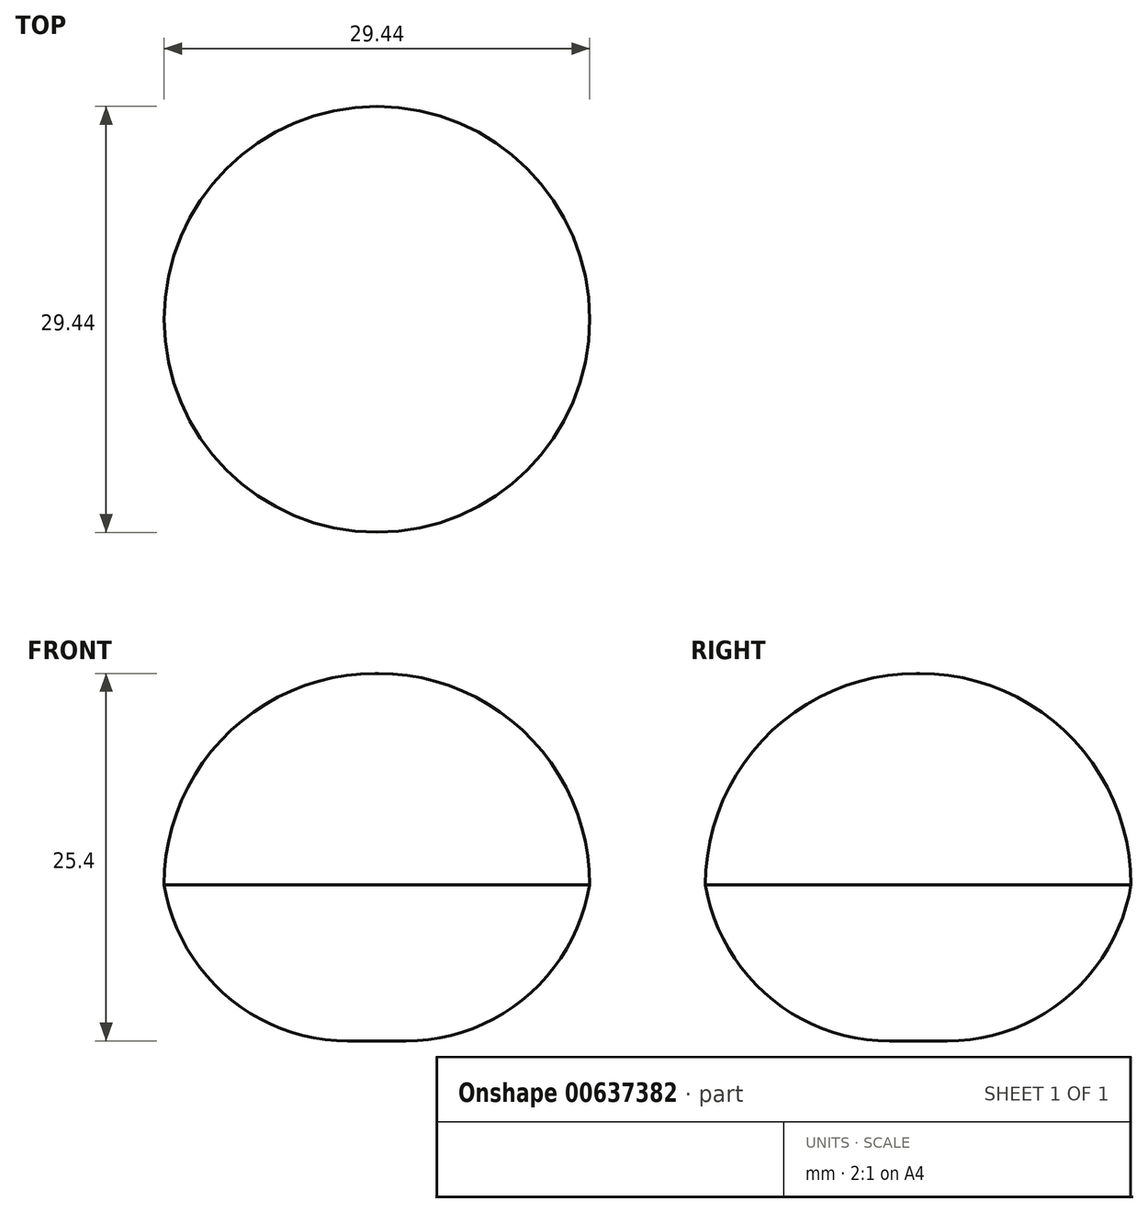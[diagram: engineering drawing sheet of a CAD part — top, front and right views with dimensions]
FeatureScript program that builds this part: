
annotation { "Feature Type Name" : "Feature", "Feature Type Description" : "" }
export const myFeature = defineFeature(function(context is Context, id is Id, definition is map)
    precondition{}
    {
        {
            var Q0;
            Q0=qCreatedBy(makeId("Top.planeOp"),FACE);
            var sketch = newSketch(context, id + "F0", { "sketchPlane" : qUnion([Q0])});
            skCircle(sketch, "E0", {"center": v(0, 0) * mm, "radius": 14.72 * mm});
            skSolve(sketch);
        }
        {
            var Q0;
            Q0=makeQuery(id+"F0.imprint","IMPRINT",FACE,{"disambiguationData":[TD([[makeQuery(id+"F0.imprint","IMPRINT",EDGE,{"derivedFrom":sQuery(id+"F0.wireOp",EDGE,"E0")}),1.0]])]});
            extrude(context, id + "F1", {"entities" : qUnion([Q0]), "depth" : 25.4 * mm, "offsetDistance" : 25.4 * mm});
        }
        {
            var Q0;
            Q0=makeQuery(id+"F1.opExtrude","CAP_EDGE",EDGE,{"disambiguationData":[OSD([sQuery(id+"F0.wireOp",EDGE,"E0")])],"isStart":false});
            fillet(context, id + "F2", {"entities" : qUnion([Q0]), "radius" : 14.6 * mm, "tangentPropagation" : true, "allowEdgeOverflow" : false});
        }
        {
            var Q0;
            Q0=makeQuery(id+"F1.opExtrude","CAP_EDGE",EDGE,{"disambiguationData":[OSD([sQuery(id+"F0.wireOp",EDGE,"E0")])],"isStart":true});
            fillet(context, id + "F3", {"entities" : qUnion([Q0]), "radius" : 12.88 * mm, "tangentPropagation" : true, "allowEdgeOverflow" : false});
        }
    });
